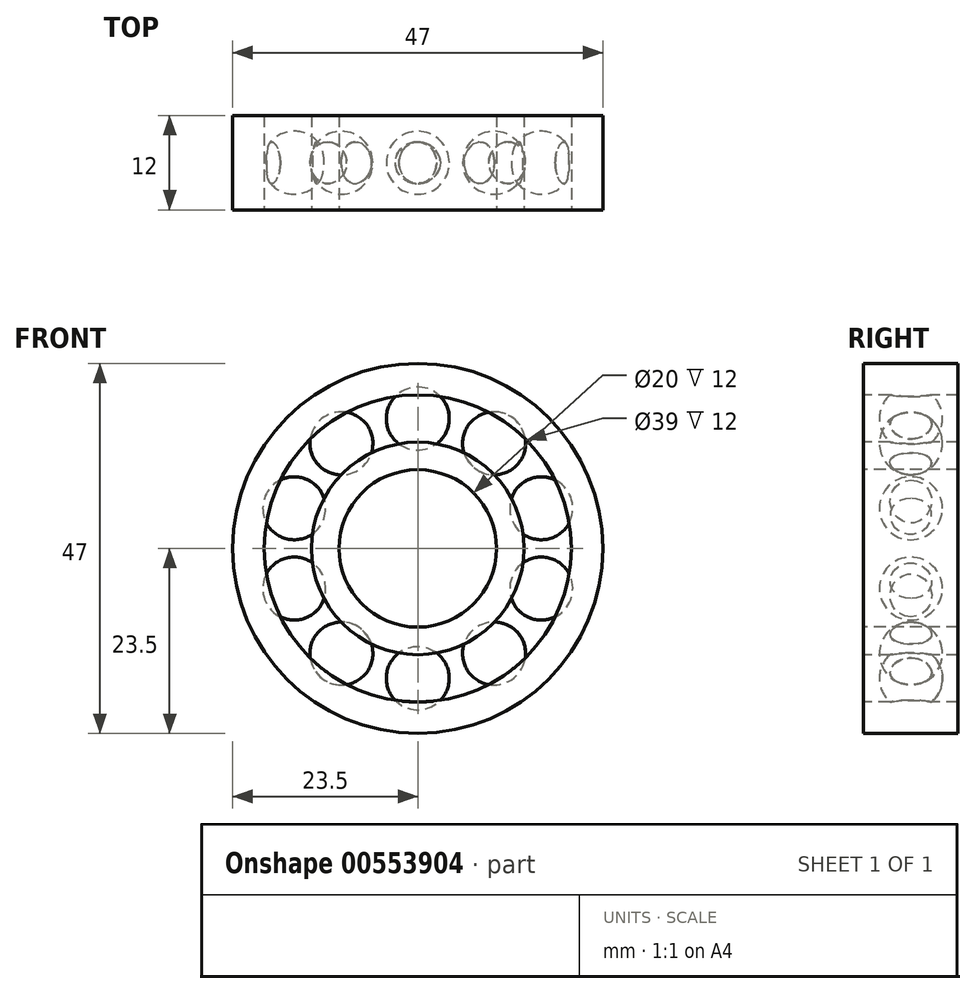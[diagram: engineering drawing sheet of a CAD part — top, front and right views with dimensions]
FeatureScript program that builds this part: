
annotation { "Feature Type Name" : "Feature", "Feature Type Description" : "" }
export const myFeature = defineFeature(function(context is Context, id is Id, definition is map)
    precondition{}
    {
        {
            var Q0;
            Q0=qCreatedBy(makeId("Right.planeOp"),FACE);
            var sketch = newSketch(context, id + "F0", { "sketchPlane" : qUnion([Q0])});
            skLineSegment(sketch, "E0.bottom", {"start": v(0, 13.5) * mm, "end": v(12, 13.5) * mm});
            skLineSegment(sketch, "E0.top", {"start": v(0, 10) * mm, "end": v(12, 10) * mm});
            skLineSegment(sketch, "E0.left", {"start": v(0, 13.5) * mm, "end": v(0, 10) * mm});
            skLineSegment(sketch, "E0.right", {"start": v(12, 13.5) * mm, "end": v(12, 10) * mm});
            skLineSegment(sketch, "E1.bottom", {"start": v(0, 23.5) * mm, "end": v(12, 23.5) * mm});
            skLineSegment(sketch, "E1.top", {"start": v(0, 19.5) * mm, "end": v(12, 19.5) * mm});
            skLineSegment(sketch, "E1.left", {"start": v(0, 23.5) * mm, "end": v(0, 19.5) * mm});
            skLineSegment(sketch, "E1.right", {"start": v(12, 23.5) * mm, "end": v(12, 19.5) * mm});
            skLineSegment(sketch, "E2", {"start": v(-16.52, 0) * mm, "end": v(20.4, 0) * mm, "construction": true});
            skSolve(sketch);
        }
        {
            var Q0;
            Q0=makeQuery(id+"F0.imprint","IMPRINT",FACE,{"disambiguationData":[TD([[makeQuery(id+"F0.imprint","IMPRINT",EDGE,{"derivedFrom":sQuery(id+"F0.wireOp",EDGE,"E1.bottom")}),-1.0]])]});
            var Q1;
            Q1=makeQuery(id+"F0.imprint","IMPRINT",FACE,{"disambiguationData":[TD([[makeQuery(id+"F0.imprint","IMPRINT",EDGE,{"derivedFrom":sQuery(id+"F0.wireOp",EDGE,"E0.bottom")}),-1.0]])]});
            var Q2;
            Q2=sQuery(id+"F0.wireOp",EDGE,"E2");
            revolve(context, id + "F1", {"entities" : qUnion([Q0, Q1]), "axis" : qUnion([Q2]), "revolveType" : RevolveType.FULL});
        }
        {
            var Q0;
            Q0=qCreatedBy(makeId("Front.planeOp"),FACE);
            cPlane(context, id + "F2", {"entities" : qUnion([Q0]), "cplaneType" : CPlaneType.OFFSET, "offset" : 6 * mm, "oppositeDirection" : true, "width" : 150 * mm, "height" : 150 * mm});
        }
        {
            var Q0;
            Q0=qCreatedBy(id+"F2.planeOp",FACE);
            var sketch = newSketch(context, id + "F3", { "sketchPlane" : qUnion([Q0])});
            skArc(sketch, "E3", {"start": v(0, 12.5) * mm, "mid": v(4, 16.5) * mm, "end": v(0, 20.5) * mm});
            skLineSegment(sketch, "E4", {"start": v(0, 22.33) * mm, "end": v(0, 9.06) * mm});
            skSolve(sketch);
        }
        {
            var Q0;
            {var subQ0=sQuery(id+"F3.wireOp",EDGE,"E3");Q0=makeQuery(id+"F3.imprint","IMPRINT",FACE,{"disambiguationData":[TD([[makeQuery(id+"F3.imprint","IMPRINT",EDGE,{"derivedFrom":subQ0}),1.0]])]});}
            var Q1;
            Q1=sQuery(id+"F3.wireOp",EDGE,"E4");
            revolve(context, id + "F4", {"entities" : qUnion([Q0]), "axis" : qUnion([Q1]), "revolveType" : RevolveType.FULL});
        }
        {
            var Q0;
            Q0=qCreatedBy(makeId("Right.planeOp"),FACE);
            var sketch = newSketch(context, id + "F5", { "sketchPlane" : qUnion([Q0])});
            skLineSegment(sketch, "E5", {"start": v(-15.75, 0) * mm, "end": v(40.02, 0) * mm, "construction": true});
            skSolve(sketch);
        }
        {
            var Q0;
            Q0=makeQuery(id+"F4.opRevolve","SWEPT_BODY",BODY,{"disambiguationData":[OSD([sQuery(id+"F3.wireOp",EDGE,"E3"),sQuery(id+"F3.wireOp",EDGE,"E4")])]});
            var Q1;
            Q1=sQuery(id+"F5.wireOp",EDGE,"E5");
            circularPattern(context, id + "F6", {"operationType" : NewBodyOperationType.ADD, "entities" : qUnion([Q0]), "axis" : qUnion([Q1]), "angle" : 360 * degree, "instanceCount" : 10, "equalSpace" : true});
        }
    });
